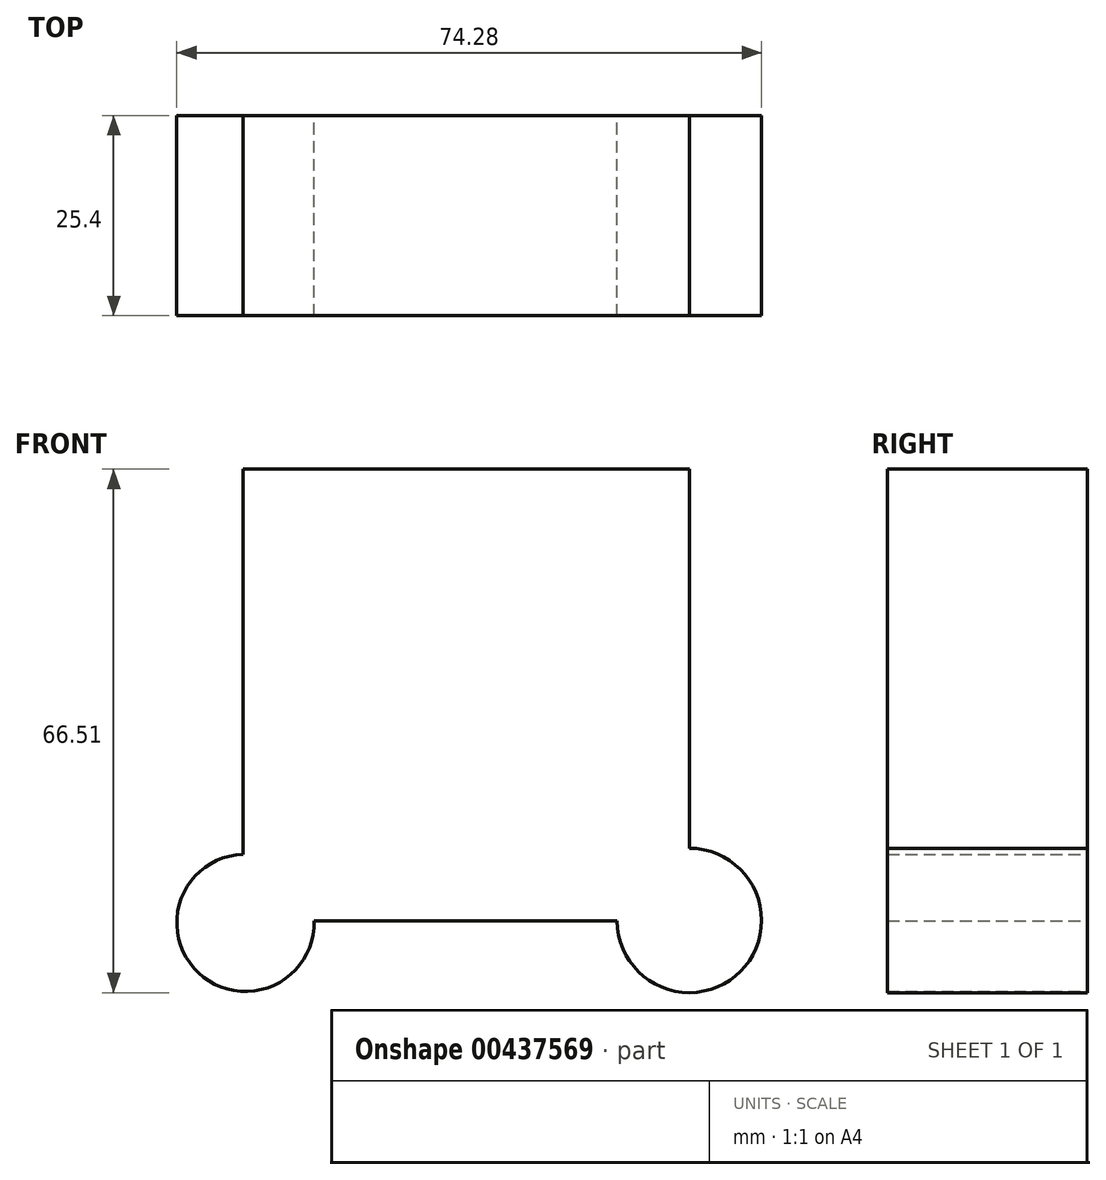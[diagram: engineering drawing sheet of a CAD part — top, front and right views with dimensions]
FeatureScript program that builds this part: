
annotation { "Feature Type Name" : "Feature", "Feature Type Description" : "" }
export const myFeature = defineFeature(function(context is Context, id is Id, definition is map)
    precondition{}
    {
        {
            var Q0;
            Q0=qCreatedBy(makeId("Front.planeOp"),FACE);
            var sketch = newSketch(context, id + "F0", { "sketchPlane" : qUnion([Q0])});
            skLineSegment(sketch, "E0.bottom", {"start": v(0, -25.2) * mm, "end": v(-56.7, -25.2) * mm});
            skLineSegment(sketch, "E0.top", {"start": v(0, 32.19) * mm, "end": v(-56.7, 32.19) * mm});
            skLineSegment(sketch, "E0.left", {"start": v(0, -25.2) * mm, "end": v(0, 32.19) * mm});
            skLineSegment(sketch, "E0.right", {"start": v(-56.7, -25.2) * mm, "end": v(-56.7, 32.19) * mm});
            skSolve(sketch);
        }
        {
            var Q0;
            Q0=makeQuery(id+"F0.imprint","IMPRINT",FACE,{"disambiguationData":[TD([[makeQuery(id+"F0.imprint","IMPRINT",EDGE,{"derivedFrom":sQuery(id+"F0.wireOp",EDGE,"E0.bottom")}),-1.0]])]});
            extrude(context, id + "F1", {"entities" : qUnion([Q0]), "depth" : 25.4 * mm});
        }
        {
            var Q0;
            Q0=qCreatedBy(makeId("Front.planeOp"),FACE);
            var sketch = newSketch(context, id + "F2", { "sketchPlane" : qUnion([Q0])});
            skCircle(sketch, "E1", {"center": v(-56.39, -25.45) * mm, "radius": 8.72 * mm});
            skCircle(sketch, "E2", {"center": v(0, -25.15) * mm, "radius": 9.17 * mm});
            skSolve(sketch);
        }
        {
            var Q0;
            Q0 = qSketchRegion(id + "F2", true);
            extrude(context, id + "F3", {"entities" : qUnion([Q0]), "operationType" : NewBodyOperationType.ADD, "depth" : 25.4 * mm});
        }
    });
